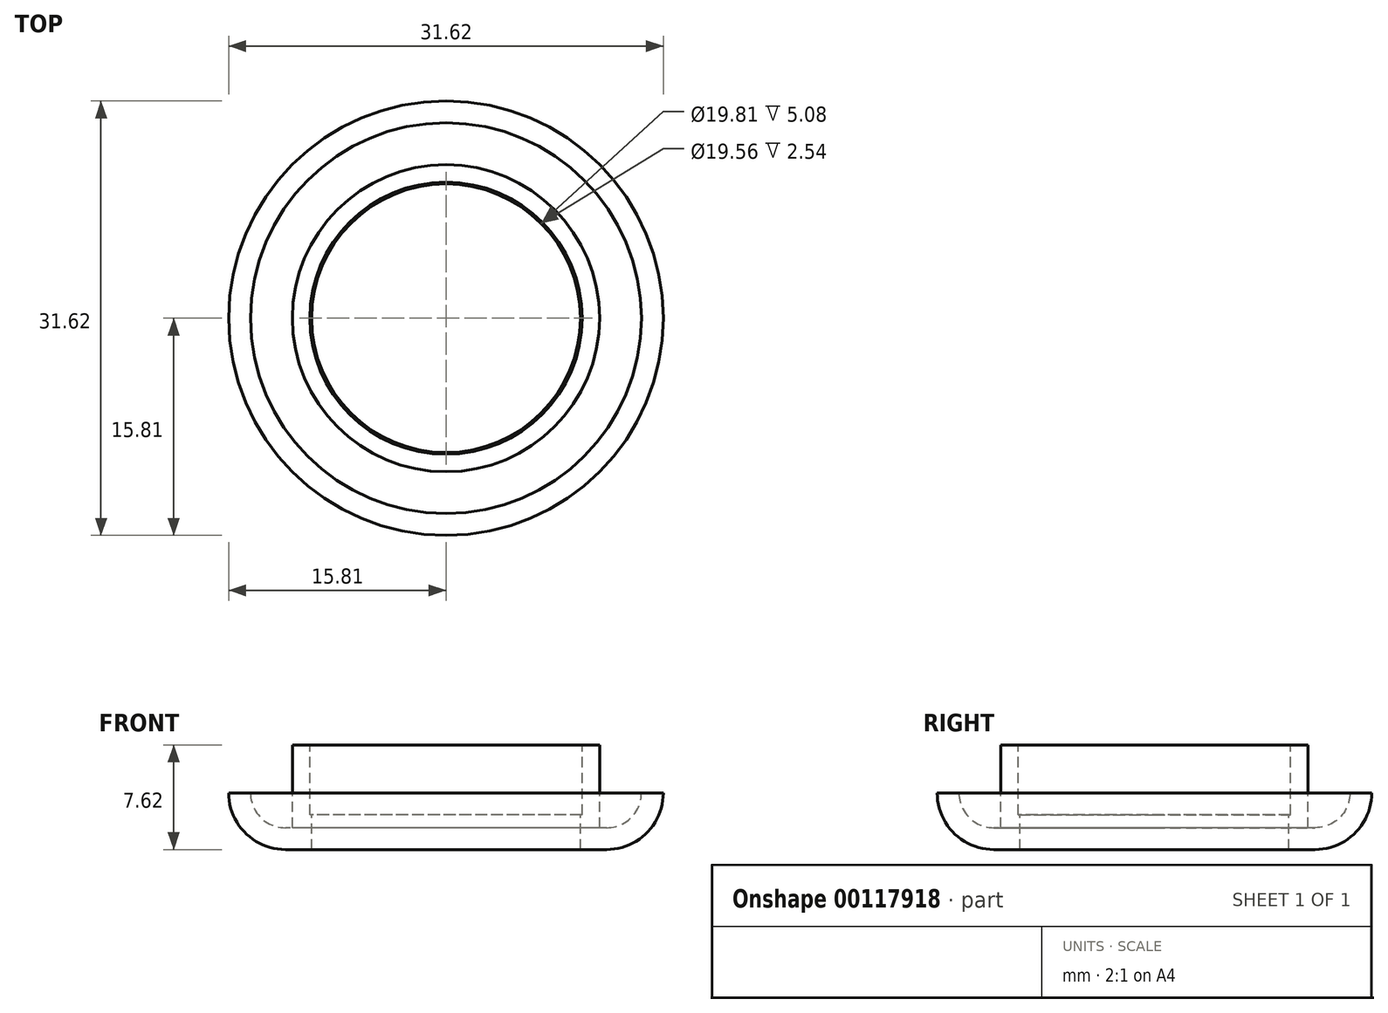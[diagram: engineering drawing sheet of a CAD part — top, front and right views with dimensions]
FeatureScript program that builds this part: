
annotation { "Feature Type Name" : "Feature", "Feature Type Description" : "" }
export const myFeature = defineFeature(function(context is Context, id is Id, definition is map)
    precondition{}
    {
        {
            var Q0;
            Q0=qCreatedBy(makeId("Front.planeOp"),FACE);
            var sketch = newSketch(context, id + "F0", { "sketchPlane" : qUnion([Q0])});
            skLineSegment(sketch, "E0", {"start": v(9.9, 7.62) * mm, "end": v(9.9, 2.54) * mm});
            skLineSegment(sketch, "E1", {"start": v(9.9, 2.54) * mm, "end": v(9.78, 2.54) * mm});
            skLineSegment(sketch, "E2", {"start": v(9.78, 2.54) * mm, "end": v(9.78, 0) * mm});
            skLineSegment(sketch, "E3", {"start": v(9.78, 0) * mm, "end": v(11.68, 0) * mm});
            skLineSegment(sketch, "E4", {"start": v(9.9, 7.62) * mm, "end": v(11.18, 7.62) * mm});
            skLineSegment(sketch, "E5", {"start": v(11.18, 7.62) * mm, "end": v(11.18, 1.59) * mm});
            skPoint(sketch, "E6", {"position": v(15.81, 4.13) * mm});
            skPoint(sketch, "E7", {"position": v(11.68, 0) * mm});
            skLineSegment(sketch, "E8", {"start": v(15.81, 4.13) * mm, "end": v(14.22, 4.13) * mm});
            skLineSegment(sketch, "E9", {"start": v(11.68, 1.59) * mm, "end": v(11.18, 1.59) * mm});
            skPoint(sketch, "E10", {"position": v(11.68, 4.13) * mm});
            skArc(sketch, "E11", {"start": v(11.68, 1.59) * mm, "mid": v(13.48, 2.33) * mm, "end": v(14.22, 4.13) * mm});
            skArc(sketch, "E12", {"start": v(11.68, 0) * mm, "mid": v(14.6, 1.2) * mm, "end": v(15.81, 4.13) * mm});
            skLineSegment(sketch, "E13", {"start": v(0, 21.97) * mm, "end": v(0, -7.95) * mm, "construction": true});
            skLineSegment(sketch, "E14", {"start": v(0, 0) * mm, "end": v(35.23, 0) * mm, "construction": true});
            skLineSegment(sketch, "E15", {"start": v(11.68, 21.9) * mm, "end": v(11.68, -7.7) * mm, "construction": true});
            skLineSegment(sketch, "E16", {"start": v(11.68, 4.13) * mm, "end": v(34.14, 4.13) * mm, "construction": true});
            skSolve(sketch);
        }
        {
            var Q0;
            Q0=makeQuery(id+"F0.imprint","IMPRINT",FACE,{"disambiguationData":[TD([[makeQuery(id+"F0.imprint","IMPRINT",EDGE,{"derivedFrom":sQuery(id+"F0.wireOp",EDGE,"E0")}),1.0]])]});
            var Q1;
            Q1=sQuery(id+"F0.wireOp",EDGE,"E13");
            revolve(context, id + "F1", {"entities" : qUnion([Q0]), "axis" : qUnion([Q1]), "revolveType" : RevolveType.FULL});
        }
    });
